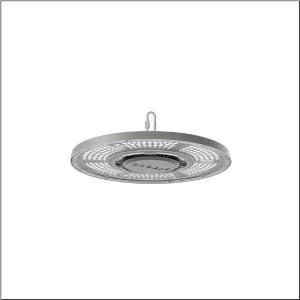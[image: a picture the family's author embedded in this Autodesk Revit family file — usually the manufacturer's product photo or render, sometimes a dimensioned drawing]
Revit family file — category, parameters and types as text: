
# Revit family: highbay_31-s_51hc417a4fmb
name_source: partatom
category: Lighting Fixtures
units: mm (PartAtom-declared; Revit-internal decimal feet)

## family parameters
Cut with Voids When Loaded = No
Host = Face
Light Source = No
Part Type = Normal
Room Calculation Point = No
Round Connector Dimension = Use Diameter
Shared = No

## types (1)
- Highbay 31-S (1 x LED, 14000 lm, 94 W, 4000K)
    Apparent Load = 94 VA
    CIE Flux Codes = 94 98 100 100 100
    Color Rendering = 80
    Color Temperature = 4000K
    Default Elevation = 1800 mm
    Description = Highbay 31-S, high bay luminaire, primary light control with lens, of PC, primary optical cover: cover panel, of PC, transparent, light emission: direct distribution, primary light characteristic: rotationally symmetric, installation type: suspended mounting, surface-mounted, LED, rated luminous flux: 14.000lm, luminous efficacy: 150lm/W, light colour: 840, colour temperature: 4000K, control gear: ON/OFF, with cable, 3x 1.0mm², free wire ends, mains connection: 220..240V, AC, 50/60Hz, cable length: 1,5m, rated input power: 94W, housing, rotationally symmetric, of diecast aluminium, powder-coated, grey aluminium (RAL 9007), with hook on luminaire side, incl. screw, diameter: 339mm, protection rating (complete): IP65, insulation class (complete): insulation class I (protective earthing), certification: CE, ENEC, UKCA, protection symbol: D, impact resistance: IK08, permissible operating ambient temperature: -30..+45°C, corresponds to IFS (International Featured Standards) requirements for safety and quality in the food industry, packaging unit: 1 piece
    Height = 141 mm
    Lamp = 1 x LED
    Lamp Light Flux = 14000 lm
    Lamp Power = 94 W
    Lamp count = 1
    Length = 339 mm
    Luminous efficacy = 149 lm/W
    Manufacturer = Siteco
    ModVariant = No
    Model = 51HC417A4FMB
    Mounting Place = Ceiling
    Mounting Type = Pendant
    Number of Poles = 1
    OnlyDefault = Yes
    Power Factor = 1
    Product Name = Highbay 31-S
    Product group = high bay luminaire
    ProductGroupID = 902
    Protection Class = Protection class I
    Protection Degree = IP 65
    RLX_Detail_Level = 1
    RLX_Emergency_Light_Flux = 0 lm
    RLX_Emergency_Type = 0
    RLX_Emergency_Type_DB = No
    RlxData = <blob elided: 106329 chars, md5=50fe1cf0>
    Socket = socket
    Standby Power = 0 W
    System Light Flux = 14000 lm
    System Power = 94 W
    Type Comments = Product without accessories
    Type Image = l_1007237.jpg
    URL = http://relux.com
    VarID = ---
    Voltage = 0 V
    Weight = 0.00 kg
    Width = 0 mm  [stored 0 ft]

note: [stored X ft] marks values corroborated as IEEE doubles in the binary element streams (Revit-internal decimal feet)

## geometry (parser evidence)
native form markers: Blend x4, Sweep x10
no freeform markers — native parametric forms only
